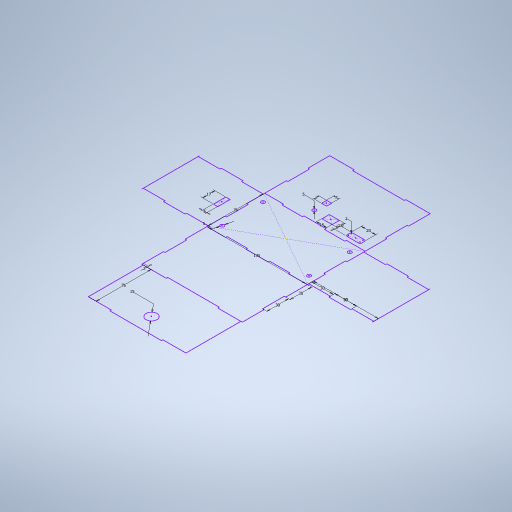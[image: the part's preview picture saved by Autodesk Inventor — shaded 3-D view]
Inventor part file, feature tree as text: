
AUTODESK INVENTOR PART (.ipt)
format: ipt  version: 2023 (Build 270158000, 158)  size: 290,304 bytes
history: native  units: in
note: dims shown in document units (in); Inventor stores cm internally (conversion verified against a paired STEP export)
features: sketch x1
ambient origin geometry x8: Origin, YZ Plane, XZ Plane, XY Plane, X Axis, Y Axis, Z Axis, Center Point
feature tree (1):
  sketch  "Sketch1"  dims[d0=5.315in d1=2.9921in d4=0.0787in d5=0.1969in d7=3.5433in d9=0.0787in d11=1.1811in d12=1.1811in d13=1.1811in d14=1.1811in d16=0.0787in d17=2.9921in d18=0.5906in d19=0.2756in d20=0.2756in d21=0.7874in d22=0.315in d23=0.2362in d24=0.6693in d25=0.1969in d26=0.0787in d27=0.5512in d28=0.3937in]
